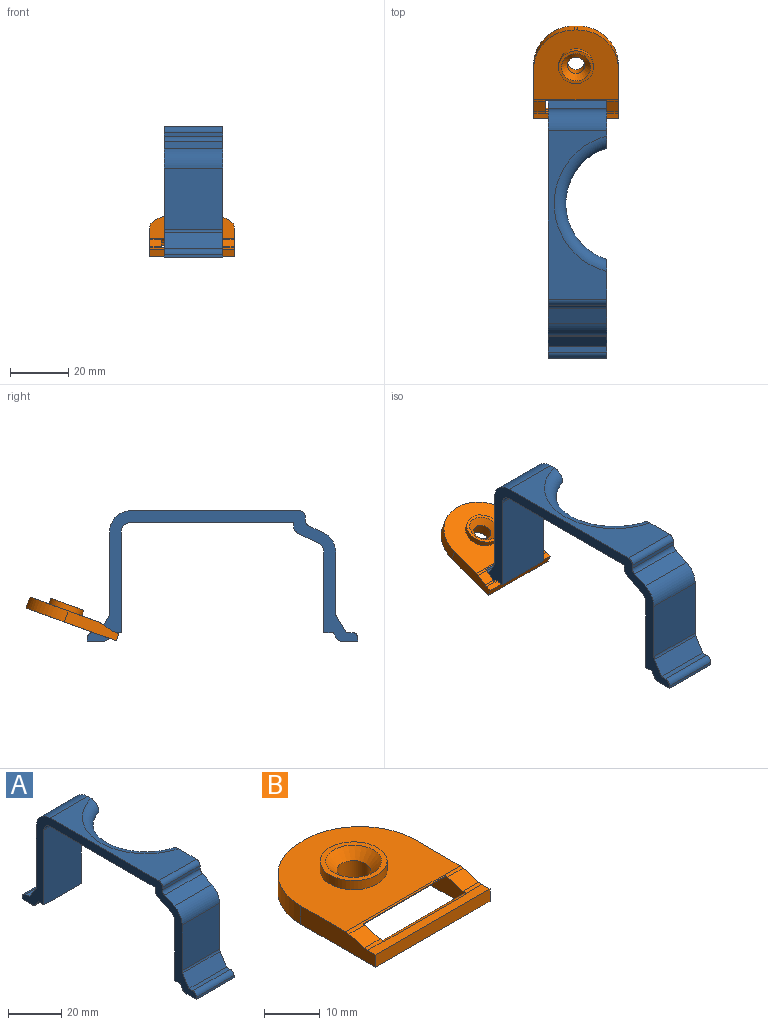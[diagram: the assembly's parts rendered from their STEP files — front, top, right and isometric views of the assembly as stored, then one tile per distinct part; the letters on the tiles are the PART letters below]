
ASSEMBLY  parts=2 mates=1
PART A: 39 faces, bbox 24.1x92.9x44.8 mm
  f0: plane 57.9x20mm, normal (0,0,1), area 538.2mm2, adj f1,f21,f27,f28,f31,f38
  f1: plane 44.8x21mm, normal (1,0,0), area 224.7mm2, adj f0,f2,f3,f4,f5,f6,f21,f22
  f2: plane 20x2.04mm, normal (0,-0.85,-0.52), area 48mm2, adj f1,f3,f28,f37
  f3: plane 20x3.12mm, normal (0,0,-1), area 62.3mm2, adj f1,f2,f4,f28
  f4: plane 34.5x20mm, normal (0,-1,0), area 690mm2, adj f1,f3,f5,f28
  f5: cylinder r=3.3mm len=20mm, axis (-1,0,0), area 103.7mm2, adj f1,f4,f6,f28
  f6: plane 55.9x20mm, normal (0,0,-1), area 726mm2, adj f1,f5,f7,f27,f28,f38
  f7: plane 20x1.23mm, normal (0,1,0), area 24.5mm2, adj f6,f27,f28,f35
  f8: plane 20x6.83mm, normal (0,0.43,-0.9), area 151.6mm2, adj f9,f27,f28,f35
  f9: cylinder r=3.3mm len=20mm, axis (-1,0,0), area 74.1mm2, adj f8,f10,f27,f28
  f10: plane 27.61x20mm, normal (0,1,0), area 552.3mm2, adj f9,f11,f27,f28
  f11: plane 20x3.12mm, normal (0,0,-1), area 62.3mm2, adj f10,f12,f27,f28
  f12: plane 20x2.04mm, normal (0,0.85,-0.52), area 48mm2, adj f11,f27,f28,f36
  f13: plane 20x5.6mm, normal (0,0,-1), area 112mm2, adj f14,f27,f28,f36
  f14: plane 20x1mm, normal (0,-1,0), area 20mm2, adj f13,f27,f28,f33
  f15: plane 20x2mm, normal (0,0,1), area 40mm2, adj f16,f27,f28,f33
  f16: plane 20x5.52mm, normal (0,-0.85,0.52), area 129.4mm2, adj f15,f27,f28,f29
  f17: plane 21.05x20mm, normal (0,-1,0), area 421mm2, adj f18,f27,f28,f29
  f18: cylinder r=7.3mm len=20mm, axis (-1,0,0), area 163.9mm2, adj f17,f19,f27,f28
  f19: plane 20x5.13mm, normal (0,-0.43,0.9), area 113.8mm2, adj f18,f27,f28,f30
  f20: plane 20x1.34mm, normal (0,-1,0), area 26.8mm2, adj f27,f28,f30,f31
  f21: cylinder r=7.3mm len=20mm, axis (-1,0,0), area 229.3mm2, adj f0,f1,f22,f28
  f22: plane 27.94x20mm, normal (0,1,0), area 558.8mm2, adj f1,f21,f28,f32
  f23: plane 20x5.52mm, normal (0,0.85,0.52), area 129.4mm2, adj f1,f24,f28,f32
  f24: plane 20x2mm, normal (0,0,1), area 40mm2, adj f1,f23,f28,f34
  f25: plane 20x1mm, normal (0,1,0), area 20mm2, adj f1,f26,f28,f34
  f26: plane 20x5.6mm, normal (0,0,-1), area 112mm2, adj f1,f25,f28,f37
  f27: plane 44.8x33.8mm, normal (1,0,0), area 265.5mm2, adj f0,f6,f7,f8,f9,f10,f11,f12
  f28: plane 92.95x44.8mm, normal (-1,0,0), area 650mm2, adj f0,f2,f3,f4,f5,f6,f7,f8
  f29: cylinder r=2mm len=20mm, axis (1,0,0), area 22mm2, adj f16,f17,f27,f28
  f30: cylinder r=2mm len=20mm, axis (1,0,0), area 44.9mm2, adj f19,f20,f27,f28
  f31: cylinder r=2mm len=20mm, axis (-1,0,0), area 62.8mm2, adj f0,f20,f27,f28
  f32: cylinder r=2mm len=20mm, axis (1,0,0), area 22mm2, adj f1,f22,f23,f28
  f33: cylinder r=2mm len=20mm, axis (-1,0,0), area 62.8mm2, adj f14,f15,f27,f28
  f34: cylinder r=2mm len=20mm, axis (-1,0,0), area 62.8mm2, adj f1,f24,f25,f28
  f35: cylinder r=3mm len=20mm, axis (-1,0,0), area 67.4mm2, adj f7,f8,f27,f28
  f36: cylinder r=2mm len=20mm, axis (-1,0,0), area 40.8mm2, adj f12,f13,f27,f28
  f37: cylinder r=2mm len=20mm, axis (-1,0,0), area 40.8mm2, adj f1,f2,f26,f28
  f38: torus R=24mm, axis (0,0,-1), area 347mm2, adj f0,f1,f6,f27
PART B: 27 faces, bbox 29x33x6 mm
  f0: plane 21x0.7mm, normal (0,0.85,0.52), area 17.2mm2, adj f10,f13,f14,f15
  f1: plane 29x2.04mm, normal (0,0,1), area 56mm2, adj f2,f9,f10,f12,f13,f14,f23,f24
  f2: plane 29x2.7mm, normal (0,-1,0), area 78.3mm2, adj f1,f3,f9,f12
  f3: plane 32.97x29mm, normal (0,0,-1), area 651.5mm2, adj f2,f4,f9,f10,f12,f13,f15,f17
  f4: plane 21x1mm, normal (0,-1,0), area 21mm2, adj f3,f7,f10,f13
  f5: plane 29x25.4mm, normal (0,0,1), area 539.2mm2, adj f9,f12,f17,f19,f22,f25,f26
  f6: plane 21x1.05mm, normal (0,0,-1), area 22mm2, adj f7,f10,f13,f16
  f7: cylinder r=2.3mm len=21mm, axis (-1,0,0), area 75.9mm2, adj f4,f6,f10,f13
  f8: plane 4x3.95mm, normal (0,-0.27,0.96), area 16.4mm2, adj f9,f10,f22,f24
  f9: plane 18.97x4mm, normal (-1,0,0), area 69.6mm2, adj f1,f2,f3,f5,f8,f22,f24,f25
  f10: plane 9.59x3.97mm, normal (1,0,0), area 27.6mm2, adj f0,f1,f3,f4,f6,f7,f8,f14
  f11: plane 4x3.95mm, normal (0,-0.27,0.96), area 16.4mm2, adj f12,f13,f22,f23
  f12: plane 18.97x4mm, normal (1,0,0), area 69.6mm2, adj f1,f2,f3,f5,f11,f22,f23,f26
  f13: plane 9.59x3.97mm, normal (-1,0,0), area 27.6mm2, adj f0,f1,f3,f4,f6,f7,f11,f14
  f14: cylinder r=1mm len=21mm, axis (1,0,0), area 21.4mm2, adj f0,f1,f10,f13
  f15: cylinder r=1mm len=21mm, axis (1,0,0), area 44.5mm2, adj f0,f3,f10,f13
  f16: cylinder r=1mm len=21mm, axis (-1,0,0), area 26mm2, adj f6,f10,f13,f22
  f17: plane 4x1mm, normal (0,1,0), area 4mm2, adj f3,f5,f25,f26
  f18: cylinder r=3mm len=6mm, axis (0,0,-1), area 75.4mm2, adj f3,f21
  f19: cylinder r=6mm len=12mm, axis (0,0,-1), area 75.4mm2, adj f5,f20
  f20: plane 12x12mm, normal (0,0,1), area 34.6mm2, adj f19,f21
  f21: cone r=3mm half-angle=45deg, axis (0,0,1), area 71.1mm2, adj f18,f20
  f22: cylinder r=3mm len=29mm, axis (-1,0,0), area 14.8mm2, adj f5,f8,f9,f10,f11,f12,f13,f16
  f23: cylinder r=3mm len=4mm, axis (-1,0,0), area 3.2mm2, adj f1,f11,f12,f13
  f24: cylinder r=3mm len=4mm, axis (1,0,0), area 3.2mm2, adj f1,f8,f9,f10
  f25: cylinder r=14mm len=14mm, axis (0,0,-1), area 88mm2, adj f3,f5,f9,f17
  f26: cylinder r=14mm len=14mm, axis (0,0,-1), area 88mm2, adj f3,f5,f12,f17
PLACE A t=(21.76,7.67,15.41)mm
PLACE B rot(axis=(1,0,0),20deg) t=(-39.24,11,3.48)mm
MATE planar B.f13 <-> A.f37  axis (-1,0,0) through (-18.24,50.26,19.54)mm
